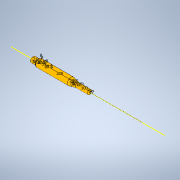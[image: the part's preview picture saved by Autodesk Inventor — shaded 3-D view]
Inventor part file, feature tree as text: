
AUTODESK INVENTOR PART (.ipt)
format: ipt  version: 2022 (Build 260153000, 153)  size: 138,752 bytes
history: native  units: mm
features: other x1, revolve x1
ambient origin geometry x8: Origin, YZ Plane, XZ Plane, XY Plane, X Axis, Y Axis, Z Axis, Center Point
bodies: Body1 (feature_tree)
feature tree (2):
  other  "Srf1"
  revolve  "RevolutionSrf1"  [1 undecoded]
note: 1 required parameter value undecoded (feature->parameter linkage not recoverable at this tier; creation-order binding heuristic only, values carry confidence <= 0.55)
